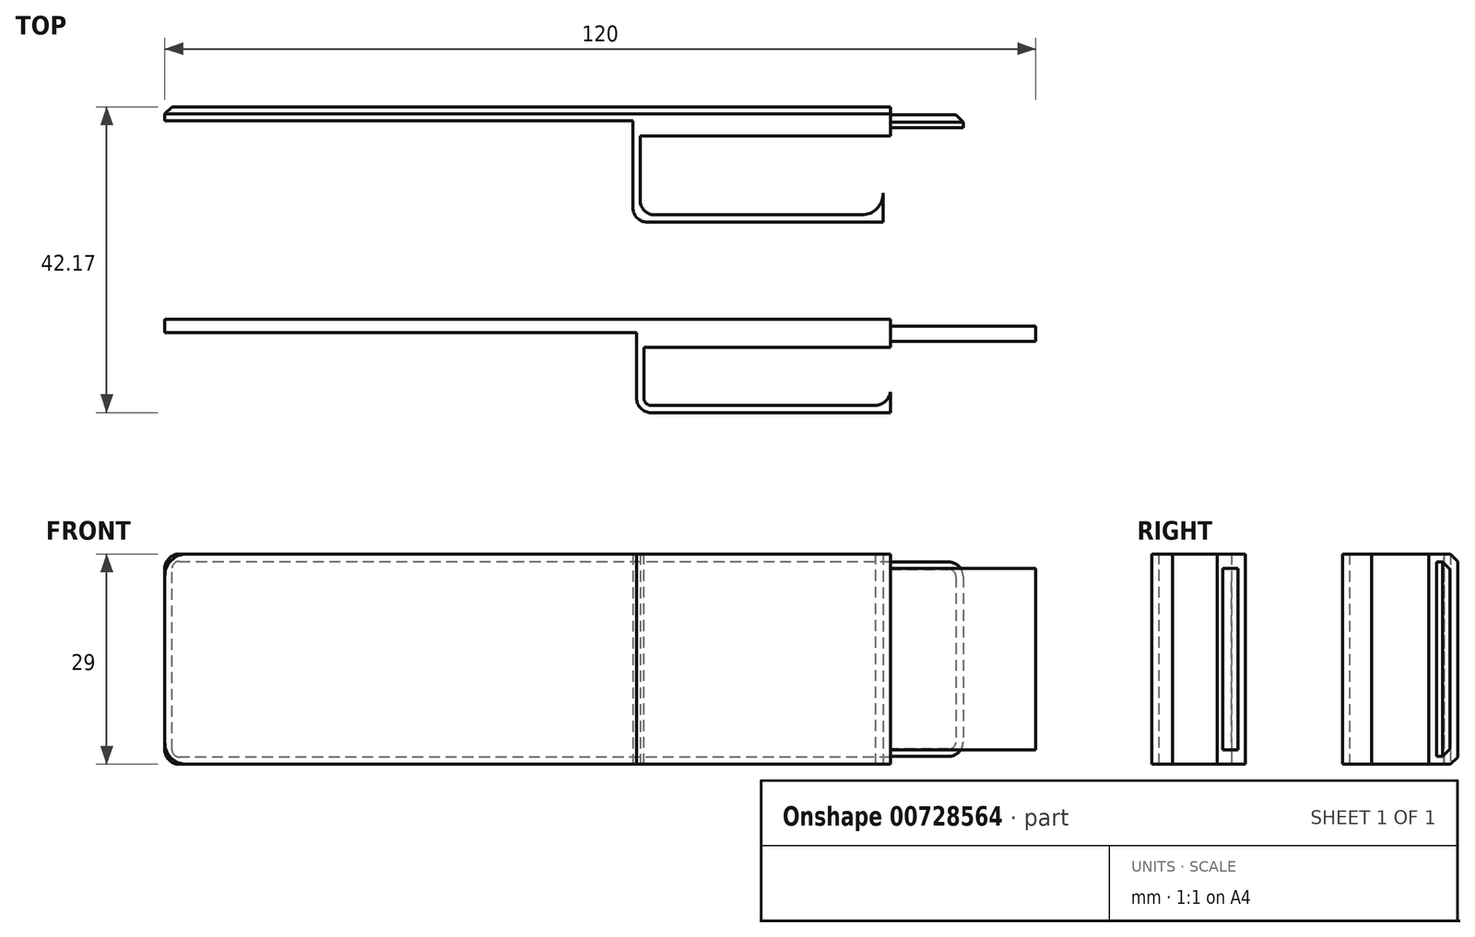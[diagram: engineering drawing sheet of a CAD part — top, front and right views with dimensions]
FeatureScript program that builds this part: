
annotation { "Feature Type Name" : "Feature", "Feature Type Description" : "" }
export const myFeature = defineFeature(function(context is Context, id is Id, definition is map)
    precondition{}
    {
        {
            var Q0;
            Q0=qCreatedBy(makeId("Front.planeOp"),FACE);
            var sketch = newSketch(context, id + "F0", { "sketchPlane" : qUnion([Q0])});
            skLineSegment(sketch, "E0.bottom", {"start": v(0, 0) * mm, "end": v(-97, 0) * mm});
            skLineSegment(sketch, "E0.top", {"start": v(0, 29) * mm, "end": v(-97, 29) * mm});
            skLineSegment(sketch, "E0.left", {"start": v(0, 0) * mm, "end": v(0, 29) * mm});
            skLineSegment(sketch, "E0.right", {"start": v(-100, 3) * mm, "end": v(-100, 26) * mm});
            skPoint(sketch, "E1.visualSharp", {"position": v(-100, 29) * mm});
            skArc(sketch, "E1.filletArc", {"start": v(-97, 29) * mm, "mid": v(-99.12, 28.12) * mm, "end": v(-100, 26) * mm});
            skPoint(sketch, "E2.visualSharp", {"position": v(-100, 0) * mm});
            skArc(sketch, "E2.filletArc", {"start": v(-100, 3) * mm, "mid": v(-99.12, 0.88) * mm, "end": v(-97, 0) * mm});
            skLineSegment(sketch, "E3", {"start": v(-35, 29) * mm, "end": v(-35, 0) * mm});
            skSolve(sketch);
        }
        {
            var Q0;
            Q0=makeQuery(id+"F0.imprint","IMPRINT",FACE,{"disambiguationData":[TD([[makeQuery(id+"F0.imprint","IMPRINT",EDGE,{"derivedFrom":sQuery(id+"F0.wireOp",EDGE,"E0.right")}),-1.0]])]});
            extrude(context, id + "F1", {"entities" : qUnion([Q0]), "depth" : 1.9 * mm, "offsetDistance" : 25 * mm});
        }
        {
            var Q0;
            {var subQ0=sQuery(id+"F0.wireOp",EDGE,"E0.left");Q0=makeQuery(id+"F0.imprint","IMPRINT",FACE,{"disambiguationData":[TD([[makeQuery(id+"F0.imprint","IMPRINT",EDGE,{"derivedFrom":subQ0}),1.0]])]});}
            extrude(context, id + "F2", {"entities" : qUnion([Q0]), "operationType" : NewBodyOperationType.ADD, "depth" : 12.9 * mm, "offsetDistance" : 25 * mm});
        }
        {
            var Q0;
            Q0=makeQuery(id+"F2.opExtrude","SWEPT_FACE",FACE,{"disambiguationData":[OSD([sQuery(id+"F0.wireOp",EDGE,"E0.left")])]});
            var sketch = newSketch(context, id + "F3", { "sketchPlane" : qUnion([Q0])});
            skLineSegment(sketch, "E4.bottom", {"start": v(-1, 27) * mm, "end": v(-3.1, 27) * mm});
            skLineSegment(sketch, "E4.top", {"start": v(-1, 2) * mm, "end": v(-3.1, 2) * mm});
            skLineSegment(sketch, "E4.left", {"start": v(-1, 27) * mm, "end": v(-1, 2) * mm});
            skLineSegment(sketch, "E4.right", {"start": v(-3.1, 27) * mm, "end": v(-3.1, 2) * mm});
            skSolve(sketch);
        }
        {
            var Q0;
            Q0=makeQuery(id+"F3.imprint","IMPRINT",FACE,{"disambiguationData":[TD([[makeQuery(id+"F3.imprint","IMPRINT",EDGE,{"derivedFrom":sQuery(id+"F3.wireOp",EDGE,"E4.bottom")}),1.0]])]});
            extrude(context, id + "F4", {"entities" : qUnion([Q0]), "operationType" : NewBodyOperationType.ADD, "depth" : 20 * mm, "offsetDistance" : 25 * mm});
        }
        {
            var Q0;
            Q0=makeQuery(id+"F2.opExtrude","CAP_EDGE",EDGE,{"disambiguationData":[OSD([sQuery(id+"F0.wireOp",EDGE,"E3")])],"isStart":false});
            fillet(context, id + "F5", {"entities" : qUnion([Q0]), "radius" : 2 * mm, "tangentPropagation" : true, "allowEdgeOverflow" : false});
        }
        {
            var Q0;
            {var subQ0=sQuery(id+"F0.wireOp",EDGE,"E0.top");Q0=makeQuery(id+"F2.boolean.opBoolean","MERGE",FACE,{"derivedFrom":[makeQuery(id+"F1.opExtrude","SWEPT_FACE",FACE,{"disambiguationData":[OSD([subQ0])]}),makeQuery(id+"F2.opExtrude","SWEPT_FACE",FACE,{"disambiguationData":[OSD([subQ0])]})]});}
            var sketch = newSketch(context, id + "F6", { "sketchPlane" : qUnion([Q0])});
            skLineSegment(sketch, "E5.0", {"start": v(-34, -10.9) * mm, "end": v(-34, -3.9) * mm});
            skArc(sketch, "E5.1", {"start": v(-34, -10.9) * mm, "mid": v(-33.7, -11.6) * mm, "end": v(-33, -11.9) * mm});
            skLineSegment(sketch, "E5.2", {"start": v(0, -11.9) * mm, "end": v(-33, -11.9) * mm});
            skLineSegment(sketch, "E6", {"start": v(-34, -3.9) * mm, "end": v(0, -3.9) * mm});
            skArc(sketch, "E7", {"start": v(-2.5, -11.9) * mm, "mid": v(-0.55, -11.16) * mm, "end": v(0, -9.16) * mm});
            skSolve(sketch);
        }
        {
            var Q0;
            Q0=makeQuery(id+"F6.imprint","IMPRINT",FACE,{"disambiguationData":[TD([[makeQuery(id+"F6.imprint","IMPRINT",EDGE,{"derivedFrom":sQuery(id+"F6.wireOp",EDGE,"E5.0")}),-1.0]])]});
            extrude(context, id + "F7", {"entities" : qUnion([Q0]), "operationType" : NewBodyOperationType.REMOVE, "oppositeDirection" : true, "depth" : 29 * mm, "offsetDistance" : 25 * mm});
        }
        {
            var Q0;
            Q0=qCreatedBy(makeId("Top.planeOp"),FACE);
            var sketch = newSketch(context, id + "F8", { "sketchPlane" : qUnion([Q0])});
            skLineSegment(sketch, "E8", {"start": v(0, 29.27) * mm, "end": v(-100, 29.27) * mm});
            skLineSegment(sketch, "E9", {"start": v(-100, 29.27) * mm, "end": v(-100, 27.37) * mm});
            skLineSegment(sketch, "E10", {"start": v(-100, 27.37) * mm, "end": v(-35.5, 27.37) * mm});
            skLineSegment(sketch, "E11", {"start": v(-35.5, 27.37) * mm, "end": v(-35.5, 15.37) * mm});
            skLineSegment(sketch, "E12", {"start": v(-33.5, 13.37) * mm, "end": v(-1, 13.37) * mm});
            skLineSegment(sketch, "E13", {"start": v(-1, 13.37) * mm, "end": v(-1, 17.37) * mm});
            skLineSegment(sketch, "E14", {"start": v(0, 29.27) * mm, "end": v(0, 25.27) * mm});
            skLineSegment(sketch, "E15", {"start": v(0, 25.27) * mm, "end": v(-34.5, 25.27) * mm});
            skLineSegment(sketch, "E16", {"start": v(-34.5, 25.27) * mm, "end": v(-34.5, 16.37) * mm});
            skLineSegment(sketch, "E17", {"start": v(-32.5, 14.37) * mm, "end": v(-4, 14.37) * mm});
            skArc(sketch, "E18", {"start": v(-4, 14.37) * mm, "mid": v(-1.88, 15.24) * mm, "end": v(-1, 17.37) * mm});
            skPoint(sketch, "E19.visualSharp", {"position": v(-34.5, 14.37) * mm});
            skArc(sketch, "E19.filletArc", {"start": v(-34.5, 16.37) * mm, "mid": v(-33.91, 14.95) * mm, "end": v(-32.5, 14.37) * mm});
            skPoint(sketch, "E20.visualSharp", {"position": v(-35.5, 13.37) * mm});
            skArc(sketch, "E20.filletArc", {"start": v(-35.5, 15.37) * mm, "mid": v(-34.91, 13.95) * mm, "end": v(-33.5, 13.37) * mm});
            skSolve(sketch);
        }
        {
            var Q0;
            Q0=makeQuery(id+"F8.imprint","IMPRINT",FACE,{"disambiguationData":[TD([[makeQuery(id+"F8.imprint","IMPRINT",EDGE,{"derivedFrom":sQuery(id+"F8.wireOp",EDGE,"E8")}),1.0]])]});
            extrude(context, id + "F9", {"entities" : qUnion([Q0]), "depth" : 29 * mm, "offsetDistance" : 25 * mm});
        }
        {
            var Q0;
            Q0=makeQuery(id+"F9.opExtrude","SWEPT_FACE",FACE,{"disambiguationData":[OSD([sQuery(id+"F8.wireOp",EDGE,"E14")])]});
            var sketch = newSketch(context, id + "F10", { "sketchPlane" : qUnion([Q0])});
            skLineSegment(sketch, "E21.0", {"start": v(26.37, 1.1) * mm, "end": v(28.17, 1.1) * mm});
            skLineSegment(sketch, "E21.1", {"start": v(26.37, 27.9) * mm, "end": v(26.37, 1.1) * mm});
            skLineSegment(sketch, "E21.2", {"start": v(28.17, 27.9) * mm, "end": v(26.37, 27.9) * mm});
            skLineSegment(sketch, "E21.3", {"start": v(28.17, 1.1) * mm, "end": v(28.17, 27.9) * mm});
            skSolve(sketch);
        }
        {
            var Q0;
            Q0=makeQuery(id+"F10.imprint","IMPRINT",FACE,{"disambiguationData":[TD([[makeQuery(id+"F10.imprint","IMPRINT",EDGE,{"derivedFrom":sQuery(id+"F10.wireOp",EDGE,"E21.0")}),1.0]])]});
            extrude(context, id + "F11", {"entities" : qUnion([Q0]), "operationType" : NewBodyOperationType.ADD, "depth" : 10 * mm, "offsetDistance" : 25 * mm});
        }
        {
            var Q0;
            Q0=makeQuery(id+"F11.opExtrude","CAP_EDGE",EDGE,{"disambiguationData":[OSD([sQuery(id+"F10.wireOp",EDGE,"E21.2")])],"isStart":false});
            var Q1;
            Q1=makeQuery(id+"F11.opExtrude","CAP_EDGE",EDGE,{"disambiguationData":[OSD([sQuery(id+"F10.wireOp",EDGE,"E21.0")])],"isStart":false});
            var Q2;
            Q2=makeQuery(id+"F9.opExtrude","CAP_EDGE",EDGE,{"disambiguationData":[OSD([sQuery(id+"F8.wireOp",EDGE,"E9")])],"isStart":false});
            var Q3;
            Q3=makeQuery(id+"F9.opExtrude","CAP_EDGE",EDGE,{"disambiguationData":[OSD([sQuery(id+"F8.wireOp",EDGE,"E9")])],"isStart":true});
            fillet(context, id + "F12", {"entities" : qUnion([Q0, Q1, Q2, Q3]), "radius" : 2 * mm, "tangentPropagation" : true, "allowEdgeOverflow" : false});
        }
        {
            var Q0;
            Q0=makeQuery(id+"F11.opExtrude","CAP_EDGE",EDGE,{"disambiguationData":[OSD([sQuery(id+"F10.wireOp",EDGE,"E21.3")])],"isStart":false});
            chamfer(context, id + "F13", {"entities" : qUnion([Q0]), "width" : 1 * mm, "tangentPropagation" : true});
        }
        {
            var Q0;
            Q0=makeQuery(id+"F9.opExtrude","SWEPT_EDGE",EDGE,{"disambiguationData":[OSD([sQuery(id+"F8.wireOp",EDGE,"E8"),sQuery(id+"F8.wireOp",EDGE,"E9")])]});
            chamfer(context, id + "F14", {"entities" : qUnion([Q0]), "width" : 1 * mm, "tangentPropagation" : true});
        }
    });
